# Revit family: S-212
name_source: partatom
category: Uniones de tubería
revit_build: Autodesk Revit 2015 (Build: 20140606_1530(x64)
units: mm (PartAtom-declared; Revit-internal decimal feet)

## types (4) — shared parameters
Aplicación = SANEAMIENTO ENTERRADO
Certificados = http://www.jimten.com
Comentarios de tipo = LIBRE DE PLOMO. FACIL DE INSTALAR GRACIAS A SU PENDIENTE INTEGRADA. SISTEMA DE ENCOLADURA. EVITE LA ACUMULACION DE SUCIEDAD EN EL INTERIOR GRACIAS A SU FONDO CUNA REDONDEADO.
Descripción = COLECTOR INSPECCION, SISTEMA COLECTOR
Entradas = 1 Ø160, 2x Ø110 MM (HEMBRA)
Fabricante = Jimten
Material = PVC (Naranja)
Modelo = S-212
Salida = Ø200 MM (HEMBRA)
URL = http://www.jimten.com

## per-type parameters (varying)
| type | A | A_Eje D-G | B | C | D | DM | E | F | G | GM | H | Referencia |
| 315x160x200 mm | 395 mm  [stored 1.29593 ft] | 120 mm  [stored 0.393701 ft] | 315 mm  [stored 1.03346 ft] | 315 mm  [stored 1.03346 ft] | 200 mm  [stored 0.656168 ft] | 215 mm | 80 mm  [stored 0.262467 ft] | 465 mm  [stored 1.52559 ft] | 160 mm  [stored 0.524934 ft] | 175 mm  [stored 0.574147 ft] | 435 mm  [stored 1.42717 ft] | 027027 |
| 250x110x160 mm | 310 mm  [stored 1.01706 ft] | 95 mm | 250 mm  [stored 0.82021 ft] | 250 mm  [stored 0.82021 ft] | 160 mm  [stored 0.524934 ft] | 175 mm  [stored 0.574147 ft] | 70 mm  [stored 0.229659 ft] | 370 mm  [stored 1.21391 ft] | 110 mm  [stored 0.360892 ft] | 125 mm  [stored 0.410105 ft] | 350 mm  [stored 1.14829 ft] | 027008 |
| 250x160x160 mm | 310 mm  [stored 1.01706 ft] | 95 mm | 250 mm  [stored 0.82021 ft] | 250 mm  [stored 0.82021 ft] | 160 mm  [stored 0.524934 ft] | 175 mm  [stored 0.574147 ft] | 70 mm  [stored 0.229659 ft] | 370 mm  [stored 1.21391 ft] | 160 mm  [stored 0.524934 ft] | 175 mm  [stored 0.574147 ft] | 350 mm  [stored 1.14829 ft] | 027049 |
| 315x200x200 mm | 395 mm  [stored 1.29593 ft] | 120 mm  [stored 0.393701 ft] | 315 mm  [stored 1.03346 ft] | 315 mm  [stored 1.03346 ft] | 200 mm  [stored 0.656168 ft] | 215 mm | 80 mm  [stored 0.262467 ft] | 465 mm  [stored 1.52559 ft] | 200 mm  [stored 0.656168 ft] | 215 mm | 435 mm  [stored 1.42717 ft] | 027050 |

note: [stored X ft] marks values corroborated as IEEE doubles in the binary element streams (Revit-internal decimal feet)
